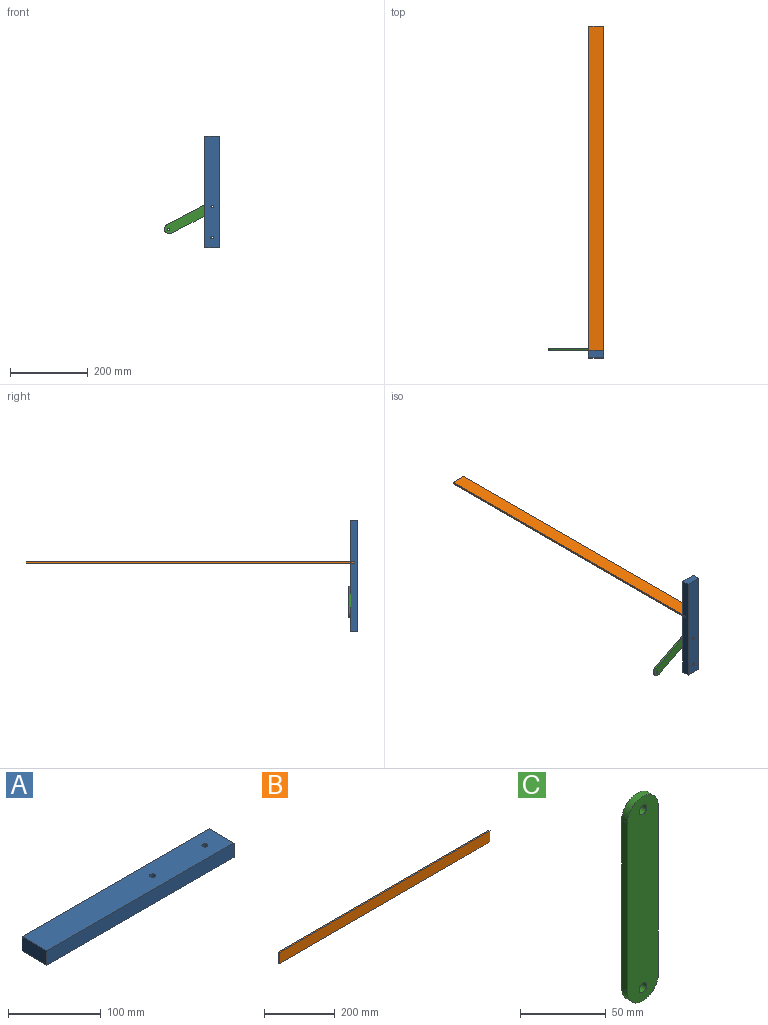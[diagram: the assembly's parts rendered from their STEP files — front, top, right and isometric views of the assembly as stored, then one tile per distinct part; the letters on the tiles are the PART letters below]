
ASSEMBLY  parts=3 mates=2
PART A: 8 faces, bbox 285.8x38.1x19.1 mm
  f0: plane 285.75x38.1mm, normal (0,0,-1), area 10823.7mm2, adj f1,f3,f4,f5,f6,f7
  f1: plane 38.1x19.05mm, normal (1,0,0), area 725.8mm2, adj f0,f2,f4,f5
  f2: plane 285.75x38.1mm, normal (0,0,1), area 10823.7mm2, adj f1,f3,f4,f5,f6,f7
  f3: plane 38.1x19.05mm, normal (-1,0,0), area 725.8mm2, adj f0,f2,f4,f5
  f4: plane 285.75x19.05mm, normal (0,-1,0), area 5443.5mm2, adj f0,f1,f2,f3
  f5: plane 285.75x19.05mm, normal (0,1,0), area 5443.5mm2, adj f0,f1,f2,f3
  f6: cylinder r=3.17mm len=19.05mm, axis (0,0,-1), area 380mm2, adj f0,f2
  f7: cylinder r=3.17mm len=19.05mm, axis (0,0,-1), area 380mm2, adj f0,f2
PART B: 6 faces, bbox 843x4.8x38.1 mm
  f0: plane 842.96x4.76mm, normal (0,0,-1), area 4014.6mm2, adj f1,f3,f4,f5
  f1: plane 38.1x4.76mm, normal (1,0,0), area 181.5mm2, adj f0,f2,f4,f5
  f2: plane 842.96x4.76mm, normal (0,0,1), area 4014.6mm2, adj f1,f3,f4,f5
  f3: plane 38.1x4.76mm, normal (-1,0,0), area 181.5mm2, adj f0,f2,f4,f5
  f4: plane 842.96x38.1mm, normal (0,-1,0), area 32116.9mm2, adj f0,f1,f2,f3
  f5: plane 842.96x38.1mm, normal (0,1,0), area 32116.9mm2, adj f0,f1,f2,f3
PART C: 8 faces, bbox 25.4x4.8x146.1 mm
  f0: plane 146.05x25.4mm, normal (0,-1,0), area 3507.9mm2, adj f2,f3,f4,f5,f6,f7
  f1: plane 146.05x25.4mm, normal (0,1,0), area 3507.9mm2, adj f2,f3,f4,f5,f6,f7
  f2: plane 120.65x4.76mm, normal (1,0,0), area 574.6mm2, adj f0,f1,f6,f7
  f3: plane 120.65x4.76mm, normal (-1,0,0), area 574.6mm2, adj f0,f1,f6,f7
  f4: cylinder r=3.17mm len=6.35mm, axis (0,1,0), area 95mm2, adj f0,f1
  f5: cylinder r=3.17mm len=6.35mm, axis (0,1,0), area 95mm2, adj f0,f1
  f6: cylinder r=12.7mm len=25.4mm, axis (0,-1,0), area 190mm2, adj f0,f1,f2,f3
  f7: cylinder r=12.7mm len=25.4mm, axis (0,-1,0), area 190mm2, adj f0,f1,f2,f3
PLACE A rot(axis=(0.58,0.58,-0.58),120deg) t=(-122.12,-67.23,-96.32)mm fixed
PLACE B rot(axis=(0.58,-0.58,-0.58),120deg) t=(-122.12,-76.75,-57.08)mm
PLACE C rot(axis=(0,-1,0),117.5deg) t=(-138.58,-62.47,-116.16)mm
MATE revolute A.f6 <-> C.f4  axis (0,1,0) through (-141.17,-67.23,-131.83)mm
MATE planar B.f0 <-> A.f5  axis (1,0,0) through (-122.12,344.73,-59.46)mm
